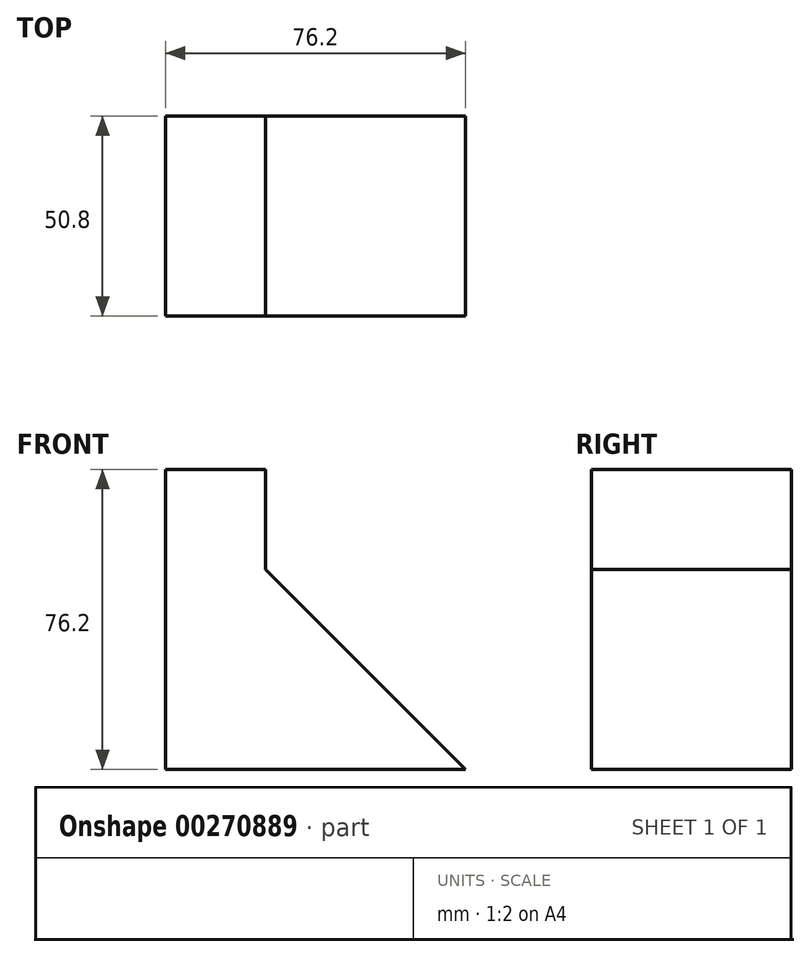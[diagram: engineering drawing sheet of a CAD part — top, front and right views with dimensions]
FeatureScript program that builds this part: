
annotation { "Feature Type Name" : "Feature", "Feature Type Description" : "" }
export const myFeature = defineFeature(function(context is Context, id is Id, definition is map)
    precondition{}
    {
        {
            var Q0;
            Q0=qCreatedBy(makeId("Front.planeOp"),FACE);
            var sketch = newSketch(context, id + "F0", { "sketchPlane" : qUnion([Q0])});
            skLineSegment(sketch, "E0", {"start": v(0, 0) * mm, "end": v(-76.2, 0) * mm});
            skLineSegment(sketch, "E1", {"start": v(-76.2, 0) * mm, "end": v(-76.2, 76.2) * mm});
            skLineSegment(sketch, "E2", {"start": v(-76.2, 76.2) * mm, "end": v(-50.8, 76.2) * mm});
            skLineSegment(sketch, "E3", {"start": v(-50.8, 76.2) * mm, "end": v(-50.8, 50.8) * mm});
            skLineSegment(sketch, "E4", {"start": v(-50.8, 50.8) * mm, "end": v(0, 0) * mm});
            skSolve(sketch);
        }
        {
            var Q0;
            Q0 = qSketchRegion(id + "F0", true);
            extrude(context, id + "F1", {"entities" : qUnion([Q0]), "depth" : 50.8 * mm});
        }
    });
